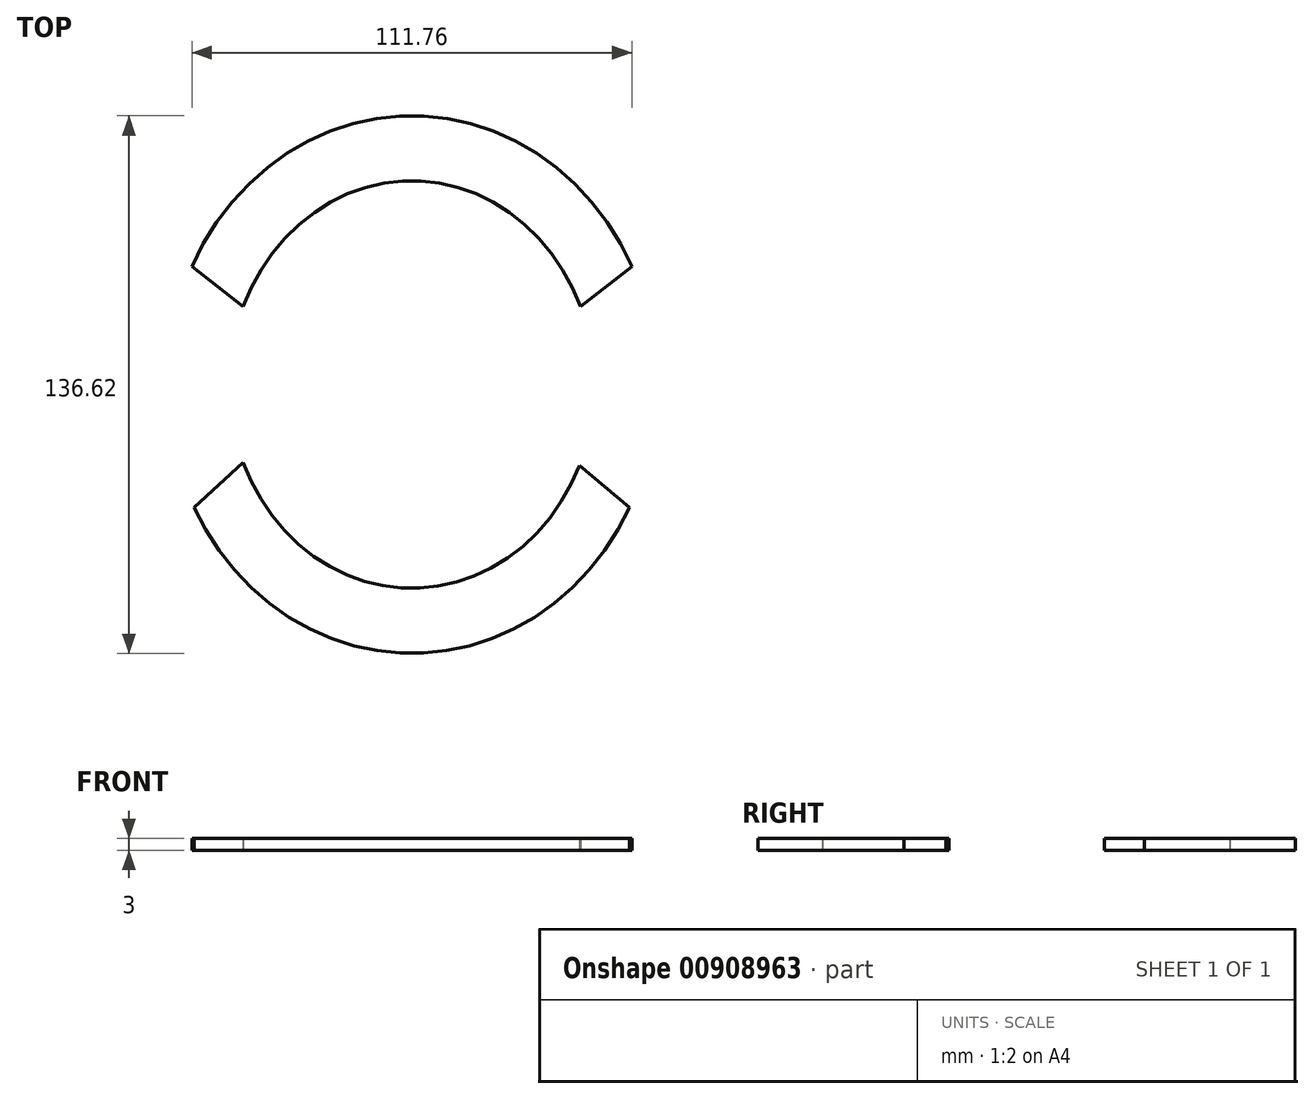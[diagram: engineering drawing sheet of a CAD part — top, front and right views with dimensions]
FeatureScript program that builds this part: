
annotation { "Feature Type Name" : "Feature", "Feature Type Description" : "" }
export const myFeature = defineFeature(function(context is Context, id is Id, definition is map)
    precondition{}
    {
        {
            var Q0;
            Q0=qCreatedBy(makeId("Top.planeOp"),FACE);
            var sketch = newSketch(context, id + "F0", { "sketchPlane" : qUnion([Q0])});
            skEllipse(sketch, "E0", {"center": v(0, 0) * mm, "majorRadius": 68.3 * mm, "minorRadius": 62.2 * mm, "majorAxis": v(0, 1)});
            skEllipse(sketch, "E1", {"center": v(0, 0) * mm, "majorRadius": 51.76 * mm, "minorRadius": 46.35 * mm, "majorAxis": v(0, 1)});
            skLineSegment(sketch, "E2", {"start": v(-42.83, 19.79) * mm, "end": v(-55.88, 29.98) * mm});
            skLineSegment(sketch, "E3", {"start": v(42.54, -20.55) * mm, "end": v(55.33, -31.2) * mm});
            skLineSegment(sketch, "E4", {"start": v(42.83, 19.79) * mm, "end": v(55.88, 29.98) * mm});
            skLineSegment(sketch, "E5", {"start": v(-42.83, -19.79) * mm, "end": v(-55.33, -31.2) * mm});
            skSolve(sketch);
        }
        {
            var Q0;
            {var subQ0=sQuery(id+"F0.wireOp",EDGE,"E2");Q0=makeQuery(id+"F0.imprint","IMPRINT",FACE,{"disambiguationData":[TD([[makeQuery(id+"F0.imprint","IMPRINT",EDGE,{"derivedFrom":subQ0}),-1.0]])]});}
            extrude(context, id + "F1", {"entities" : qUnion([Q0]), "depth" : 3 * mm, "offsetDistance" : 25 * mm});
        }
        {
            var Q0;
            {var subQ0=sQuery(id+"F0.wireOp",EDGE,"E3");Q0=makeQuery(id+"F0.imprint","IMPRINT",FACE,{"disambiguationData":[TD([[makeQuery(id+"F0.imprint","IMPRINT",EDGE,{"derivedFrom":subQ0}),-1.0]])]});}
            extrude(context, id + "F2", {"entities" : qUnion([Q0]), "depth" : 3 * mm, "offsetDistance" : 25 * mm});
        }
    });
